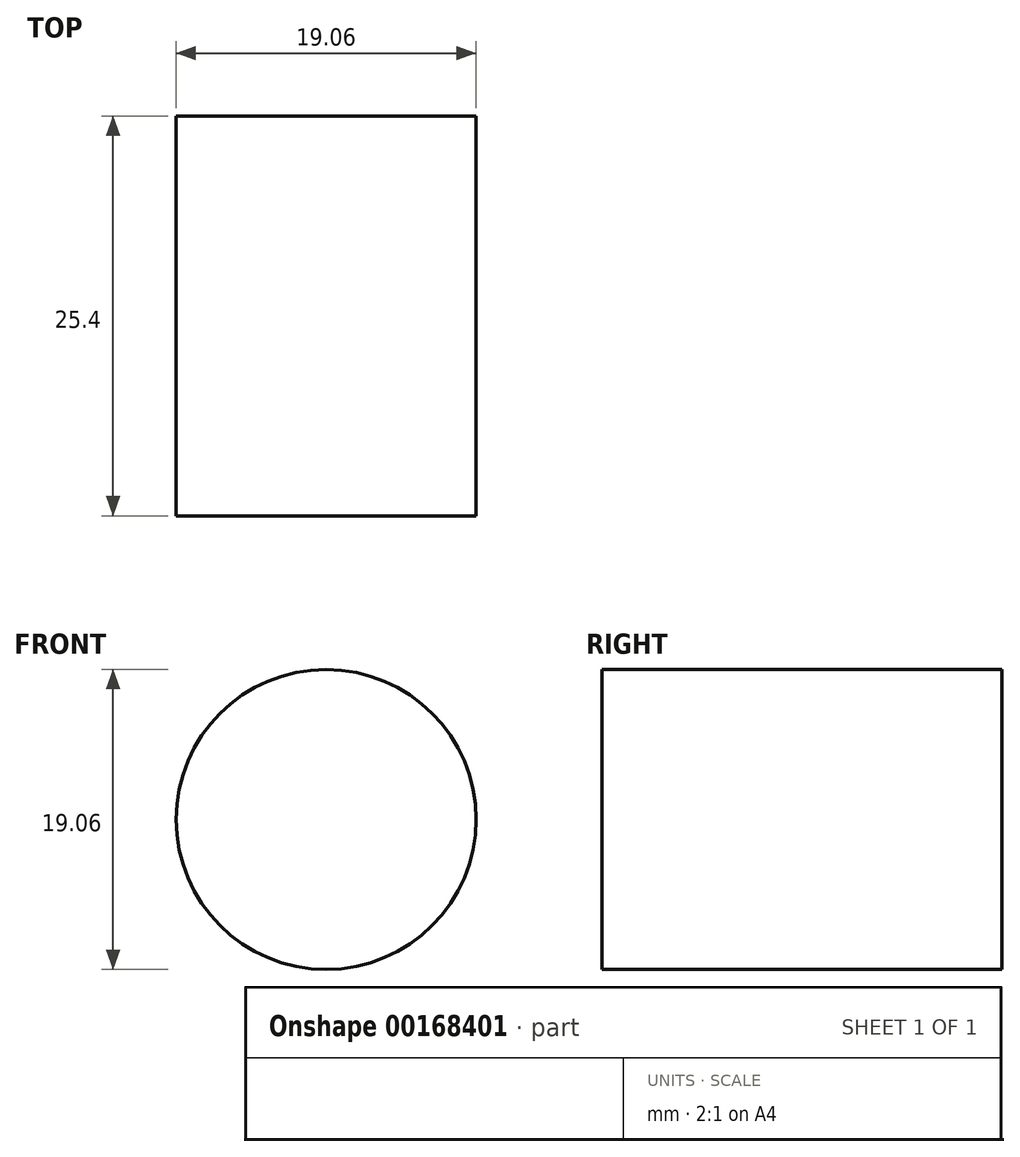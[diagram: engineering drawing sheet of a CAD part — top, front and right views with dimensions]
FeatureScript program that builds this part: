
annotation { "Feature Type Name" : "Feature", "Feature Type Description" : "" }
export const myFeature = defineFeature(function(context is Context, id is Id, definition is map)
    precondition{}
    {
        {
            var Q0;
            Q0=qCreatedBy(makeId("Front.planeOp"),FACE);
            var sketch = newSketch(context, id + "F0", { "sketchPlane" : qUnion([Q0])});
            skCircle(sketch, "E0", {"center": v(0, 0) * mm, "radius": 9.53 * mm});
            skSolve(sketch);
        }
        {
            var Q0;
            Q0 = qSketchRegion(id + "F0", true);
            extrude(context, id + "F1", {"entities" : qUnion([Q0]), "depth" : 25.4 * mm});
        }
        {
            var Q0;
            Q0=qCreatedBy(makeId("Front.planeOp"),FACE);
            var sketch = newSketch(context, id + "F2", { "sketchPlane" : qUnion([Q0])});
            skLineSegment(sketch, "E1.bottom", {"start": v(4.76, 4.76) * mm, "end": v(-4.76, 4.76) * mm});
            skLineSegment(sketch, "E1.top", {"start": v(4.76, -4.76) * mm, "end": v(-4.76, -4.76) * mm});
            skLineSegment(sketch, "E1.left", {"start": v(4.76, 4.76) * mm, "end": v(4.76, -4.76) * mm});
            skLineSegment(sketch, "E1.right", {"start": v(-4.76, 4.76) * mm, "end": v(-4.76, -4.76) * mm});
            skPoint(sketch, "E1.middle", {"position": v(0, 0) * mm});
            skCircle(sketch, "E2", {"center": v(0, 0) * mm, "radius": 4.62 * mm});
            skSolve(sketch);
        }
        {
            var Q0;
            Q0 = qSketchRegion(id + "F2", true);
            extrude(context, id + "F3", {"entities" : qUnion([Q0]), "operationType" : NewBodyOperationType.REMOVE, "endBound" : BoundingType.THROUGH_ALL, "oppositeDirection" : true, "depth" : 25.4 * mm});
        }
    });
